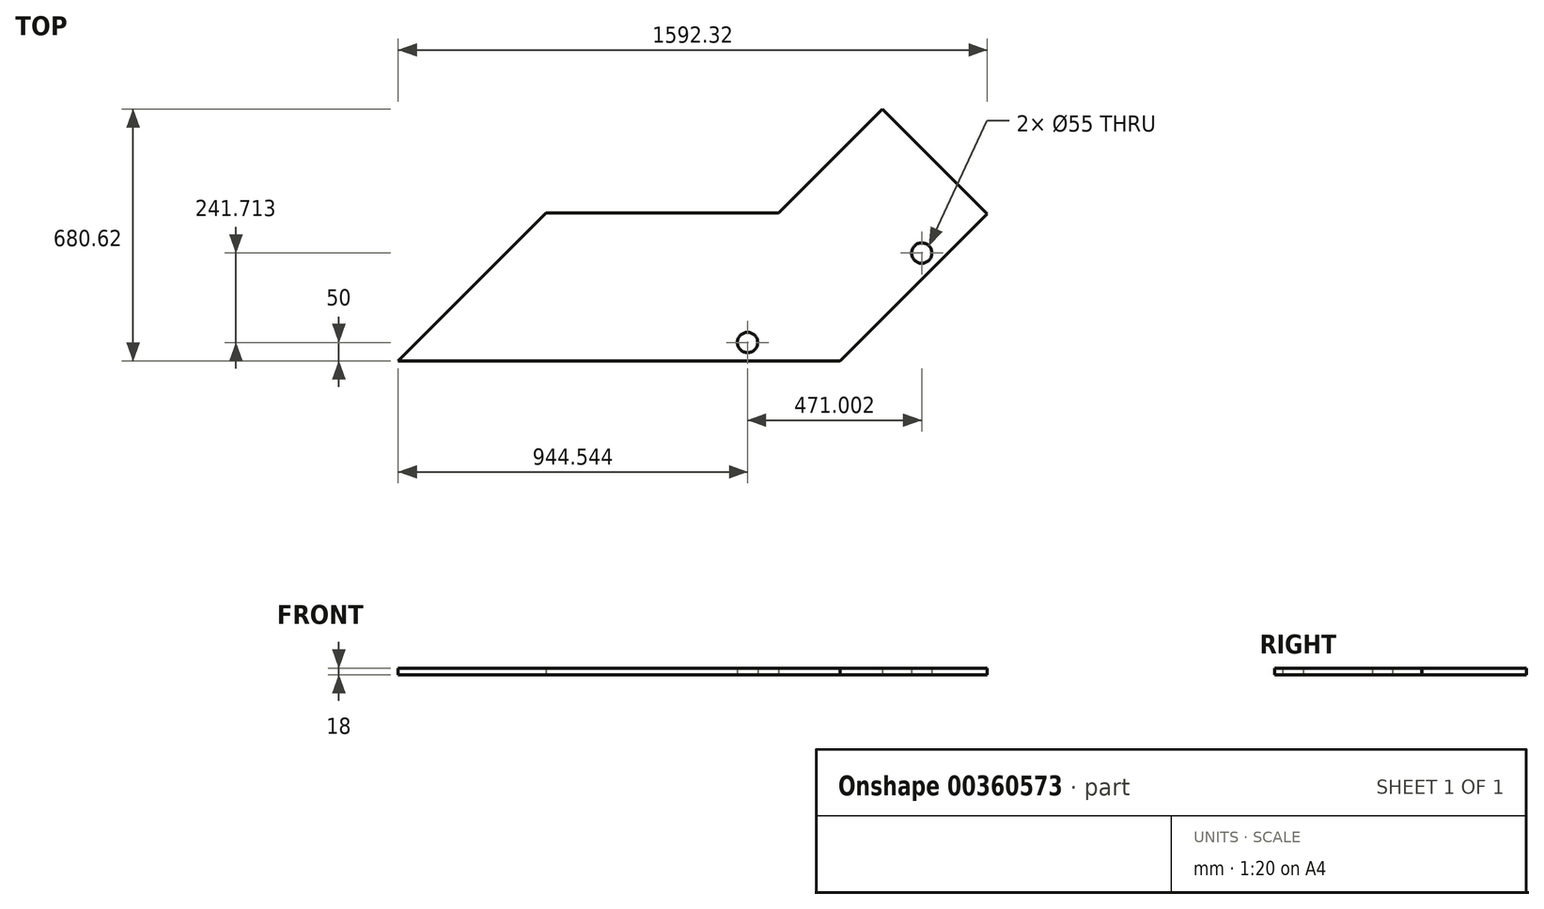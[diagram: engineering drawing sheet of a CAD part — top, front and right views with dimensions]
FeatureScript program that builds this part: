
annotation { "Feature Type Name" : "Feature", "Feature Type Description" : "" }
export const myFeature = defineFeature(function(context is Context, id is Id, definition is map)
    precondition{}
    {
        {
            var Q0;
            Q0=qCreatedBy(makeId("Top.planeOp"),FACE);
            var sketch = newSketch(context, id + "F0", { "sketchPlane" : qUnion([Q0])});
            skLineSegment(sketch, "E0", {"start": v(0, 0) * mm, "end": v(1194.54, 0) * mm});
            skLineSegment(sketch, "E1", {"start": v(1194.54, 0) * mm, "end": v(1592.32, 397.78) * mm});
            skLineSegment(sketch, "E2", {"start": v(400, 400) * mm, "end": v(0, 0) * mm});
            skLineSegment(sketch, "E3", {"start": v(1592.32, 397.78) * mm, "end": v(1309.48, 680.62) * mm});
            skLineSegment(sketch, "E4", {"start": v(1309.48, 680.62) * mm, "end": v(1028.86, 400) * mm});
            skLineSegment(sketch, "E5", {"start": v(1028.86, 400) * mm, "end": v(400, 400) * mm});
            skLineSegment(sketch, "E6", {"start": v(1605.05, 385.05) * mm, "end": v(1202, -18) * mm, "construction": true});
            skLineSegment(sketch, "E7", {"start": v(1202, -18) * mm, "end": v(-18, -18) * mm, "construction": true});
            skLineSegment(sketch, "E8", {"start": v(-30.73, -5.27) * mm, "end": v(374.54, 400) * mm, "construction": true});
            skLineSegment(sketch, "E9", {"start": v(-30.73, -5.27) * mm, "end": v(-18, -18) * mm, "construction": true});
            skLineSegment(sketch, "E10", {"start": v(-18, -18) * mm, "end": v(-18, -18) * mm});
            skCircle(sketch, "E11", {"center": v(944.54, 50) * mm, "radius": 27.5 * mm});
            skCircle(sketch, "E12", {"center": v(1415.55, 291.71) * mm, "radius": 27.5 * mm});
            skSolve(sketch);
        }
        {
            var Q0;
            Q0=makeQuery(id+"F0.imprint","IMPRINT",FACE,{"disambiguationData":[TD([[makeQuery(id+"F0.imprint","IMPRINT",EDGE,{"derivedFrom":sQuery(id+"F0.wireOp",EDGE,"E0")}),1.0]])]});
            extrude(context, id + "F1", {"entities" : qUnion([Q0]), "depth" : 18 * mm});
        }
    });
